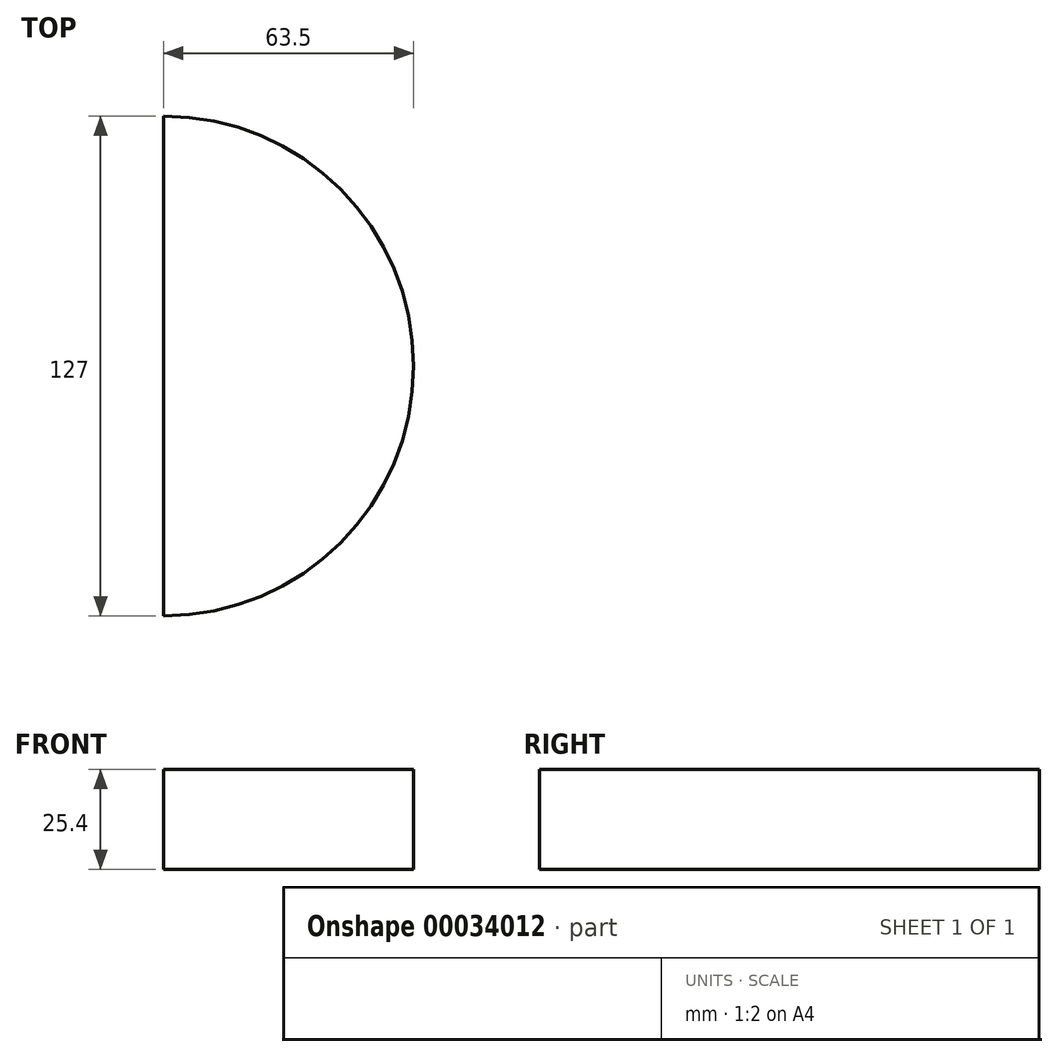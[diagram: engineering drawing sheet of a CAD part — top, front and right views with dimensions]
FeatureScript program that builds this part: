
annotation { "Feature Type Name" : "Feature", "Feature Type Description" : "" }
export const myFeature = defineFeature(function(context is Context, id is Id, definition is map)
    precondition{}
    {
        {
            var Q0;
            Q0=qCreatedBy(makeId("Top.planeOp"),FACE);
            var sketch = newSketch(context, id + "F0", { "sketchPlane" : qUnion([Q0])});
            skCircle(sketch, "E0", {"center": v(0, 0) * mm, "radius": 63.5 * mm});
            skLineSegment(sketch, "E1", {"start": v(0, 63.5) * mm, "end": v(0, -68.58) * mm});
            skSolve(sketch);
        }
        {
            var Q0;
            {var subQ0=sQuery(id+"F0.wireOp",EDGE,"E1");var subQ1=sQuery(id+"F0.wireOp",EDGE,"E0");var subQ3=makeQuery(id+"F0.imprint","INTERSECT",VERTEX,{"disambiguationData":[OD(0.0)],"derivedFrom":[subQ1,subQ0]});Q0=makeQuery(id+"F0.imprint","IMPRINT",FACE,{"disambiguationData":[TD([[makeQuery(id+"F0.imprint","IMPRINT",EDGE,{"disambiguationData":[TD([[subQ3,-1.0]])],"derivedFrom":subQ1}),1.0]])]});}
            extrude(context, id + "F1", {"entities" : qUnion([Q0]), "depth" : 25.4 * mm});
        }
    });
